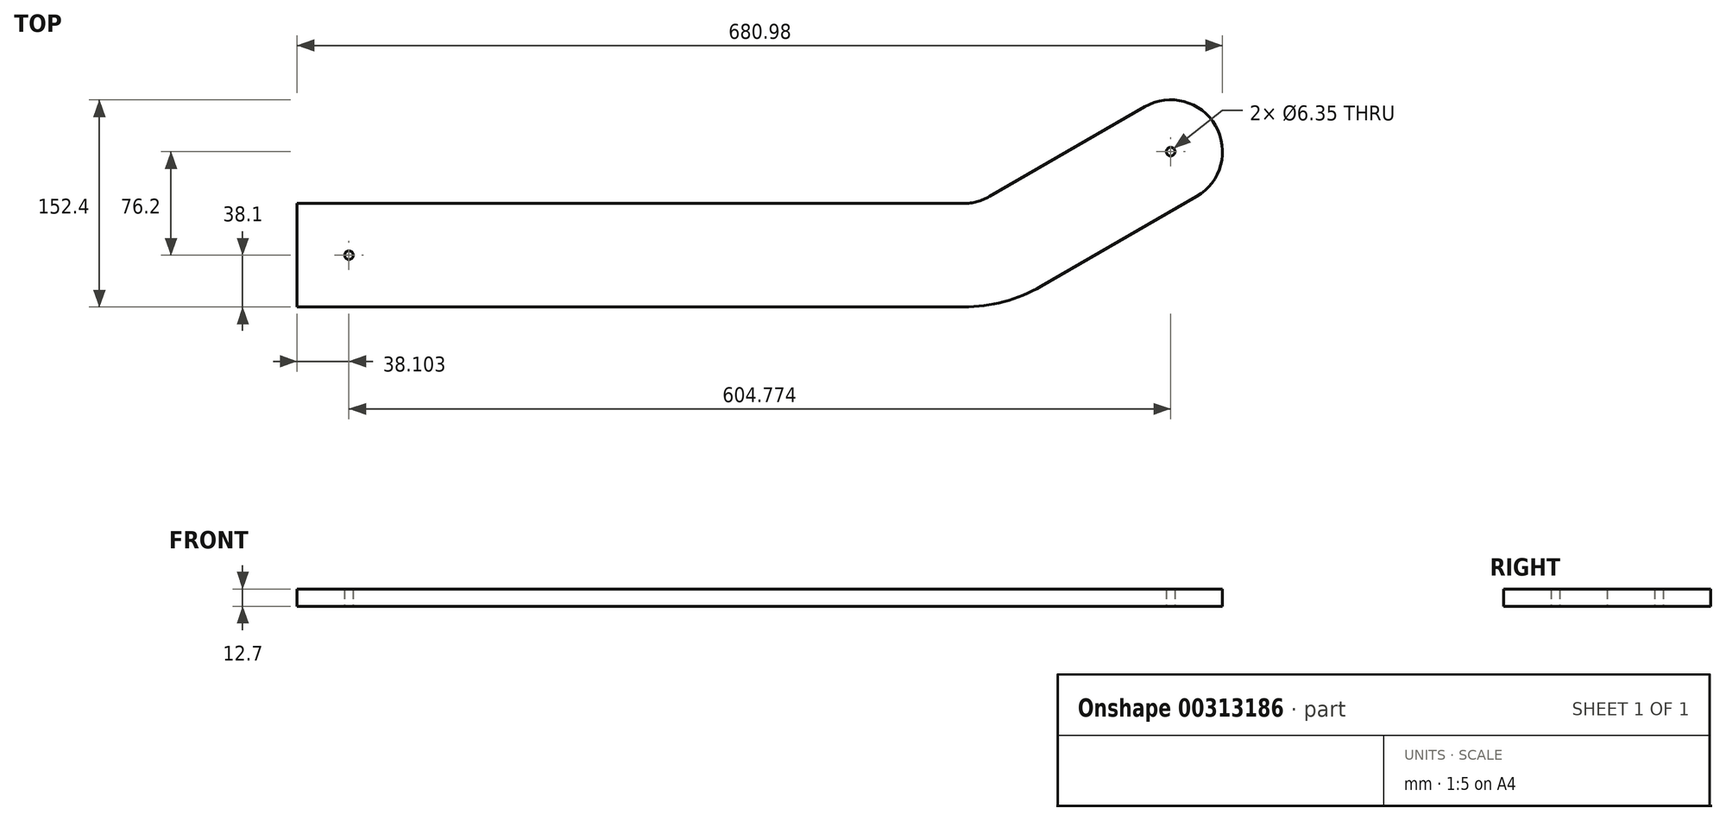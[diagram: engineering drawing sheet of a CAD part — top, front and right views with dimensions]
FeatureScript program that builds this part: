
annotation { "Feature Type Name" : "Feature", "Feature Type Description" : "" }
export const myFeature = defineFeature(function(context is Context, id is Id, definition is map)
    precondition{}
    {
        {
            var Q0;
            Q0=qCreatedBy(makeId("Top.planeOp"),FACE);
            var sketch = newSketch(context, id + "F0", { "sketchPlane" : qUnion([Q0])});
            skLineSegment(sketch, "E0.bottom", {"start": v(-245.24, 38.1) * mm, "end": v(245.24, 38.1) * mm});
            skLineSegment(sketch, "E0.top", {"start": v(-245.24, -38.1) * mm, "end": v(245.24, -38.1) * mm});
            skLineSegment(sketch, "E0.left", {"start": v(-245.24, 38.1) * mm, "end": v(-245.24, -38.1) * mm});
            skPoint(sketch, "E0.middle", {"position": v(0, 0) * mm});
            skLineSegment(sketch, "E1.0", {"start": v(-245.24, 76.2) * mm, "end": v(321.44, 76.2) * mm});
            skArc(sketch, "E2", {"start": v(245.24, 38.1) * mm, "mid": v(255.1, 39.4) * mm, "end": v(264.29, 43.2) * mm});
            skArc(sketch, "E3", {"start": v(245.24, -38.1) * mm, "mid": v(274.82, -34.2) * mm, "end": v(302.39, -22.79) * mm});
            skLineSegment(sketch, "E4", {"start": v(283.34, 10.2) * mm, "end": v(397.64, 76.2) * mm});
            skPoint(sketch, "E5.orphan", {"position": v(359.54, 76.2) * mm});
            skPoint(sketch, "E6.orphan", {"position": v(245.24, -55.78) * mm});
            skArc(sketch, "E7.trimOffspring", {"start": v(245.24, -38.1) * mm, "mid": v(274.82, -34.2) * mm, "end": v(302.39, -22.79) * mm, "construction": true});
            skPoint(sketch, "E8.orphan", {"position": v(207.14, 10.2) * mm});
            skArc(sketch, "E9.trimOffspring", {"start": v(245.24, 38.1) * mm, "mid": v(255.1, 39.4) * mm, "end": v(264.29, 43.2) * mm, "construction": true});
            skArc(sketch, "E10", {"start": v(283.34, 10.2) * mm, "mid": v(264.96, 2.6) * mm, "end": v(245.24, 0) * mm});
            skLineSegment(sketch, "E11.0", {"start": v(264.29, 43.2) * mm, "end": v(378.59, 109.2) * mm});
            skLineSegment(sketch, "E12.0", {"start": v(302.39, -22.79) * mm, "end": v(416.69, 43.2) * mm});
            skArc(sketch, "E13", {"start": v(378.59, 109.2) * mm, "mid": v(430.63, 95.25) * mm, "end": v(416.69, 43.2) * mm});
            skLineSegment(sketch, "E14", {"start": v(245.24, -38.1) * mm, "end": v(245.24, -84.2) * mm, "construction": true});
            skPoint(sketch, "E15.middle", {"position": v(-245.24, -38.1) * mm});
            skPoint(sketch, "E15.bottom.end.orphan", {"position": v(-283.34, -76.2) * mm});
            skPoint(sketch, "E16.orphan", {"position": v(-207.14, -76.2) * mm});
            skCircle(sketch, "E17", {"center": v(-207.14, 0) * mm, "radius": 3.18 * mm});
            skPoint(sketch, "E18.trimOffspring.end.orphan", {"position": v(-283.34, 0) * mm});
            skPoint(sketch, "E19", {"position": v(435.74, 76.2) * mm});
            skText(sketch, "E20", { "text": "1/2\" birch plywood", "fontName": "OpenSans-Regular.ttf"});
            skPoint(sketch, "E21.end.orphan", {"position": v(397.64, 114.3) * mm});
            skPoint(sketch, "E22.end.orphan", {"position": v(430.63, 95.25) * mm});
            skCircle(sketch, "E23", {"center": v(397.64, 76.2) * mm, "radius": 3.18 * mm});
            const initialGuessF0  = {"E20": [-0.18626, -0.20863, 1, 0, 0.03347]};
            skSetInitialGuess(sketch, initialGuessF0);
            skSolve(sketch);
        }
        {
            var Q0;
            {var subQ0=sQuery(id+"F0.wireOp",EDGE,"E21");Q0=makeQuery(id+"F0.imprint","IMPRINT",FACE,{"disambiguationData":[TD([[makeQuery(id+"F0.imprint","IMPRINT",EDGE,{"derivedFrom":subQ0}),1.0]])]});}
            var Q1;
            {var subQ0=sQuery(id+"F0.wireOp",EDGE,"E21");Q1=makeQuery(id+"F0.imprint","IMPRINT",FACE,{"disambiguationData":[TD([[makeQuery(id+"F0.imprint","IMPRINT",EDGE,{"derivedFrom":subQ0}),-1.0]])]});}
            var Q2;
            {var subQ0=sQuery(id+"F0.wireOp",EDGE,"E2");Q2=makeQuery(id+"F0.imprint","IMPRINT",FACE,{"disambiguationData":[TD([[makeQuery(id+"F0.imprint","IMPRINT",EDGE,{"derivedFrom":subQ0}),-1.0]])]});}
            var Q3;
            {var subQ0=sQuery(id+"F0.wireOp",EDGE,"E3");Q3=makeQuery(id+"F0.imprint","IMPRINT",FACE,{"disambiguationData":[TD([[makeQuery(id+"F0.imprint","IMPRINT",EDGE,{"derivedFrom":subQ0}),1.0]])]});}
            var Q4;
            {var subQ0=sQuery(id+"F0.wireOp",EDGE,"E4");Q4=makeQuery(id+"F0.imprint","IMPRINT",FACE,{"disambiguationData":[TD([[makeQuery(id+"F0.imprint","IMPRINT",EDGE,{"derivedFrom":subQ0}),1.0]])]});}
            var Q5;
            {var subQ2=sQuery(id+"F0.wireOp",EDGE,"E4");Q5=makeQuery(id+"F0.imprint","IMPRINT",FACE,{"disambiguationData":[TD([[makeQuery(id+"F0.imprint","IMPRINT",EDGE,{"derivedFrom":subQ2}),-1.0]])]});}
            var Q6;
            {var subQ1=sQuery(id+"F0.wireOp",EDGE,"E0.bottom");Q6=makeQuery(id+"F0.imprint","IMPRINT",FACE,{"disambiguationData":[TD([[makeQuery(id+"F0.imprint","IMPRINT",EDGE,{"derivedFrom":subQ1}),-1.0]])]});}
            var Q7;
            Q7=sQuery(id+"F0.wireOp",EDGE,"E11.0");
            var Q8;
            Q8=sQuery(id+"F0.wireOp",EDGE,"E13");
            var Q9;
            Q9=sQuery(id+"F0.wireOp",EDGE,"E12.0");
            var Q10;
            Q10=sQuery(id+"F0.wireOp",EDGE,"E3");
            var Q11;
            Q11=sQuery(id+"F0.wireOp",EDGE,"E0.top");
            var Q12;
            Q12=sQuery(id+"F0.wireOp",EDGE,"E0.left");
            var Q13;
            Q13=sQuery(id+"F0.wireOp",EDGE,"E0.bottom");
            var Q14;
            Q14=sQuery(id+"F0.wireOp",EDGE,"E2");
            extrude(context, id + "F1", {"entities" : qUnion([Q0, Q1, Q2, Q3, Q4, Q5, Q6]), "surfaceEntities" : qUnion([Q7, Q8, Q9, Q10, Q11, Q12, Q13, Q14]), "endBound" : BoundingType.SYMMETRIC, "depth" : 12.7 * mm});
        }
    });
